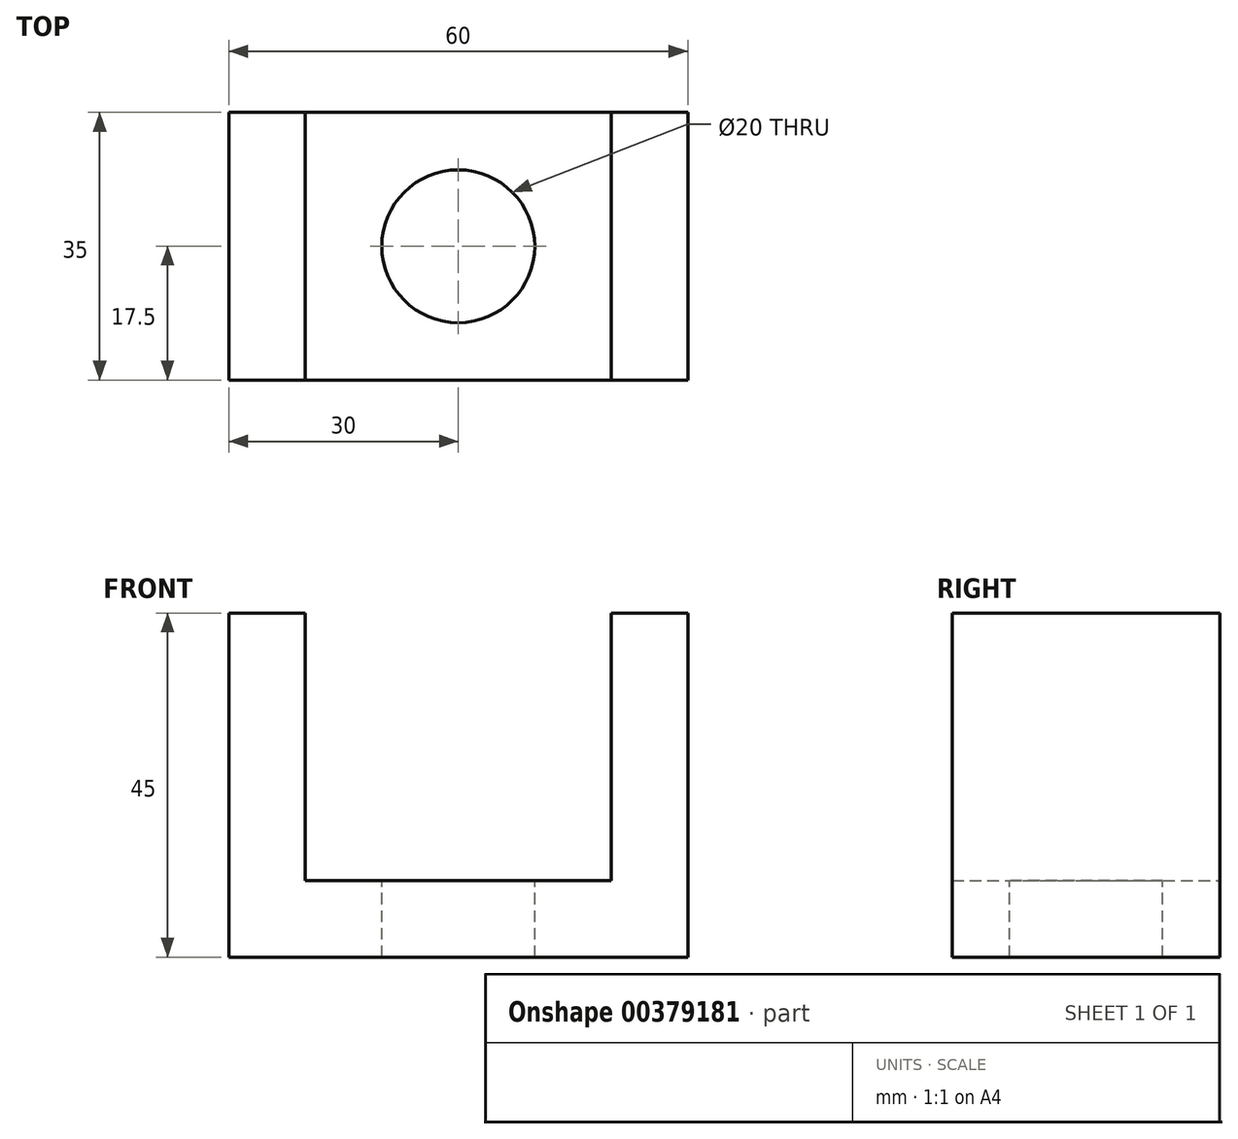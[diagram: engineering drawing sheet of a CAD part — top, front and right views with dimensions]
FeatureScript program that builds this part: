
annotation { "Feature Type Name" : "Feature", "Feature Type Description" : "" }
export const myFeature = defineFeature(function(context is Context, id is Id, definition is map)
    precondition{}
    {
        {
            var Q0;
            Q0=qCreatedBy(makeId("Front.planeOp"),FACE);
            var sketch = newSketch(context, id + "F0", { "sketchPlane" : qUnion([Q0])});
            skLineSegment(sketch, "E0", {"start": v(0, 0) * mm, "end": v(60, 0) * mm});
            skLineSegment(sketch, "E1", {"start": v(60, 0) * mm, "end": v(60, 45) * mm});
            skLineSegment(sketch, "E2", {"start": v(60, 45) * mm, "end": v(50, 45) * mm});
            skLineSegment(sketch, "E3", {"start": v(50, 45) * mm, "end": v(50, 10) * mm});
            skLineSegment(sketch, "E4", {"start": v(50, 10) * mm, "end": v(10, 10) * mm});
            skLineSegment(sketch, "E5", {"start": v(10, 10) * mm, "end": v(10, 45) * mm});
            skLineSegment(sketch, "E6", {"start": v(10, 45) * mm, "end": v(0, 45) * mm});
            skLineSegment(sketch, "E7", {"start": v(0, 45) * mm, "end": v(0, 0) * mm});
            skSolve(sketch);
        }
        {
            var Q0;
            Q0 = qSketchRegion(id + "F0", true);
            extrude(context, id + "F1", {"entities" : qUnion([Q0]), "depth" : 35 * mm});
        }
        {
            var Q0;
            Q0=makeQuery(id+"F1.opExtrude","SWEPT_FACE",FACE,{"disambiguationData":[OSD([sQuery(id+"F0.wireOp",EDGE,"E4")])]});
            var sketch = newSketch(context, id + "F2", { "sketchPlane" : qUnion([Q0])});
            skCircle(sketch, "E8", {"center": v(30, -17.5) * mm, "radius": 10 * mm});
            skPoint(sketch, "E8.centerSnap0", {"position": v(50, -17.5) * mm});
            skSolve(sketch);
        }
        {
            var Q0;
            Q0=makeQuery(id+"F2.imprint","IMPRINT",FACE,{"disambiguationData":[TD([[makeQuery(id+"F2.imprint","IMPRINT",EDGE,{"derivedFrom":sQuery(id+"F2.wireOp",EDGE,"E8")}),1.0]])]});
            extrude(context, id + "F3", {"entities" : qUnion([Q0]), "operationType" : NewBodyOperationType.REMOVE, "endBound" : BoundingType.THROUGH_ALL, "oppositeDirection" : true, "depth" : 25 * mm});
        }
    });
